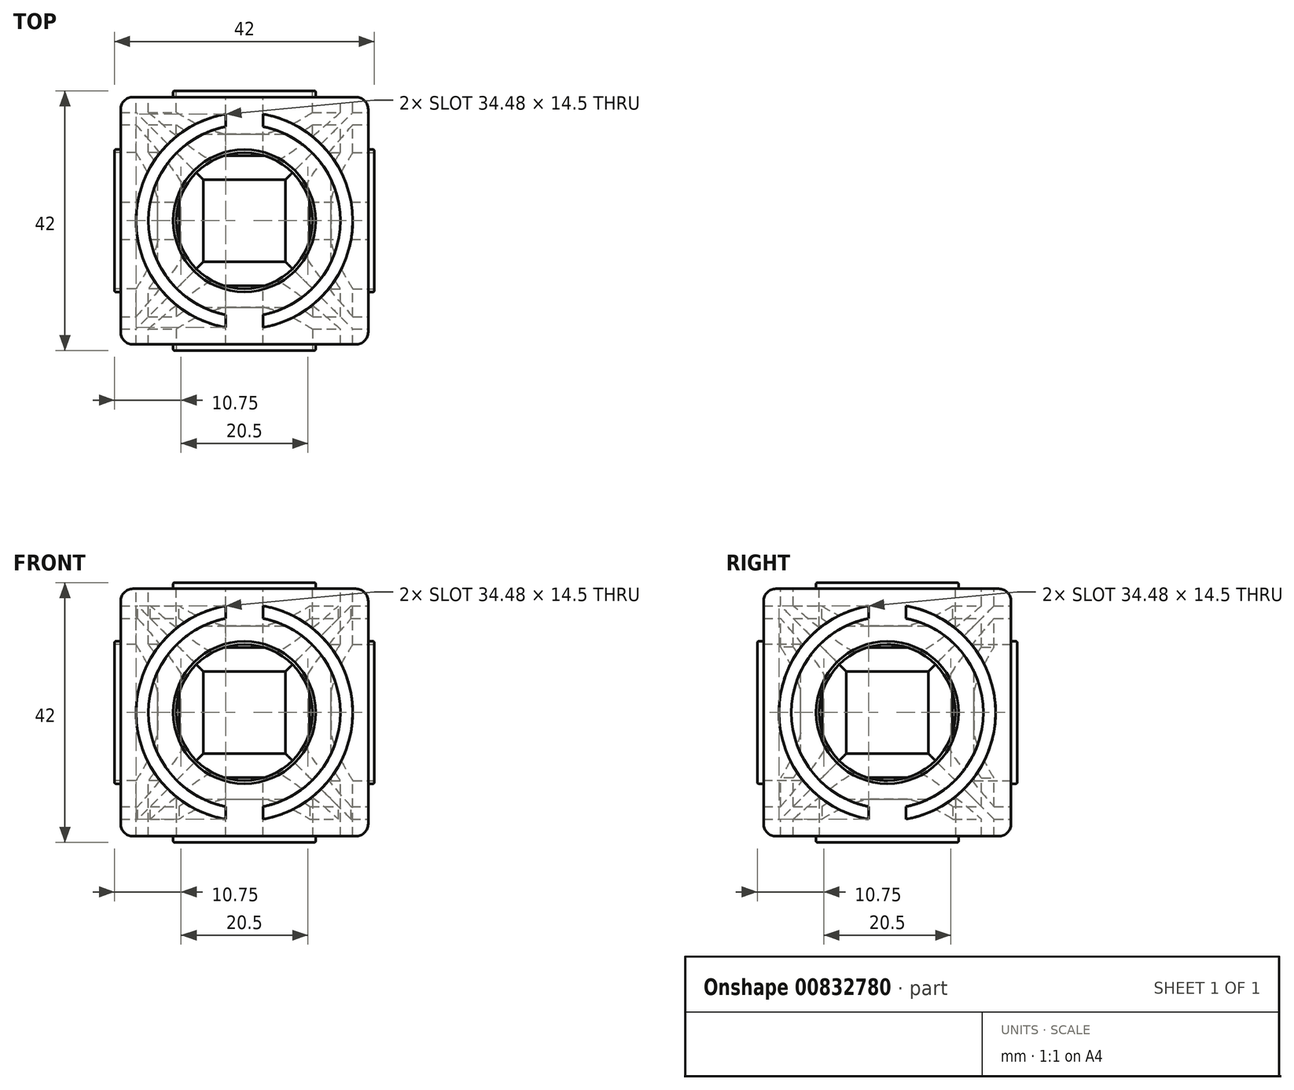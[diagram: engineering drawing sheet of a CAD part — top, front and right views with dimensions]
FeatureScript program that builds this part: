
annotation { "Feature Type Name" : "Feature", "Feature Type Description" : "" }
export const myFeature = defineFeature(function(context is Context, id is Id, definition is map)
    precondition{}
    {
        {
            var Q0;
            Q0=qCreatedBy(makeId("Top.planeOp"),FACE);
            var sketch = newSketch(context, id + "F0", { "sketchPlane" : qUnion([Q0])});
            skLineSegment(sketch, "E0", {"start": v(0, 20) * mm, "end": v(20, 20) * mm});
            skLineSegment(sketch, "E1", {"start": v(20, 20) * mm, "end": v(20, 0) * mm});
            skLineSegment(sketch, "E2", {"start": v(20, 0) * mm, "end": v(20, -20) * mm});
            skLineSegment(sketch, "E3.MirrorCS", {"start": v(-20, 0) * mm, "end": v(-20, -20) * mm});
            skLineSegment(sketch, "E4.MirrorCS", {"start": v(0, 20) * mm, "end": v(-20, 20) * mm});
            skLineSegment(sketch, "E5.MirrorCS", {"start": v(-20, -20) * mm, "end": v(0, -20) * mm});
            skLineSegment(sketch, "E6.MirrorCS", {"start": v(-20, 20) * mm, "end": v(-20, 0) * mm});
            skPoint(sketch, "E7.end.orphan", {"position": v(0, -20) * mm});
            skLineSegment(sketch, "E8.MirrorCS", {"start": v(20, -20) * mm, "end": v(0, -20) * mm});
            skSolve(sketch);
        }
        {
            var Q0;
            Q0 = qSketchRegion(id + "F0", true);
            extrude(context, id + "F1", {"entities" : qUnion([Q0]), "depth" : 40 * mm, "offsetDistance" : 25 * mm});
        }
        {
            var Q0;
            Q0=makeQuery(id+"F1.opExtrude","CAP_FACE",FACE,{"disambiguationData":[OSD([sQuery(id+"F0.wireOp",EDGE,"E0"),sQuery(id+"F0.wireOp",EDGE,"E1"),sQuery(id+"F0.wireOp",EDGE,"E2"),sQuery(id+"F0.wireOp",EDGE,"E3.MirrorCS"),sQuery(id+"F0.wireOp",EDGE,"E4.MirrorCS"),sQuery(id+"F0.wireOp",EDGE,"E5.MirrorCS"),sQuery(id+"F0.wireOp",EDGE,"E6.MirrorCS"),sQuery(id+"F0.wireOp",EDGE,"E8.MirrorCS")])],"isStart":true});
            var sketch = newSketch(context, id + "F2", { "sketchPlane" : qUnion([Q0])});
            skCircle(sketch, "E9", {"center": v(0, 0) * mm, "radius": 11 * mm});
            skSolve(sketch);
        }
        {
            var Q0;
            Q0 = qSketchRegion(id + "F2", true);
            extrude(context, id + "F3", {"entities" : qUnion([Q0]), "operationType" : NewBodyOperationType.REMOVE, "oppositeDirection" : true, "depth" : 6 * mm, "offsetDistance" : 25 * mm});
        }
        {
            var Q0;
            Q0=makeQuery(id+"F1.opExtrude","CAP_FACE",FACE,{"disambiguationData":[OSD([sQuery(id+"F0.wireOp",EDGE,"E0"),sQuery(id+"F0.wireOp",EDGE,"E1"),sQuery(id+"F0.wireOp",EDGE,"E2"),sQuery(id+"F0.wireOp",EDGE,"E3.MirrorCS"),sQuery(id+"F0.wireOp",EDGE,"E4.MirrorCS"),sQuery(id+"F0.wireOp",EDGE,"E5.MirrorCS"),sQuery(id+"F0.wireOp",EDGE,"E6.MirrorCS"),sQuery(id+"F0.wireOp",EDGE,"E8.MirrorCS")])],"isStart":false});
            var sketch = newSketch(context, id + "F4", { "sketchPlane" : qUnion([Q0])});
            skCircle(sketch, "E10", {"center": v(0, 0) * mm, "radius": 11 * mm});
            skSolve(sketch);
        }
        {
            var Q0;
            Q0 = qSketchRegion(id + "F4", true);
            extrude(context, id + "F5", {"entities" : qUnion([Q0]), "operationType" : NewBodyOperationType.REMOVE, "oppositeDirection" : true, "depth" : 6 * mm, "offsetDistance" : 25 * mm});
        }
        {
            var Q0;
            Q0=makeQuery(id+"F1.opExtrude","SWEPT_FACE",FACE,{"disambiguationData":[OSD([sQuery(id+"F0.wireOp",EDGE,"E5.MirrorCS"),sQuery(id+"F0.wireOp",EDGE,"E8.MirrorCS")])]});
            var sketch = newSketch(context, id + "F6", { "sketchPlane" : qUnion([Q0])});
            skCircle(sketch, "E11", {"center": v(0, 20) * mm, "radius": 11 * mm});
            skPoint(sketch, "E12.orphan", {"position": v(-20, 20) * mm});
            skPoint(sketch, "E13.end.orphan", {"position": v(20, 20) * mm});
            skPoint(sketch, "E14.start.orphan", {"position": v(0, 40) * mm});
            skSolve(sketch);
        }
        {
            var Q0;
            Q0 = qSketchRegion(id + "F6", true);
            extrude(context, id + "F7", {"entities" : qUnion([Q0]), "operationType" : NewBodyOperationType.REMOVE, "oppositeDirection" : true, "depth" : 6 * mm, "offsetDistance" : 25 * mm});
        }
        {
            var Q0;
            Q0=makeQuery(id+"F1.opExtrude","SWEPT_FACE",FACE,{"disambiguationData":[OSD([sQuery(id+"F0.wireOp",EDGE,"E1"),sQuery(id+"F0.wireOp",EDGE,"E2")])]});
            var sketch = newSketch(context, id + "F8", { "sketchPlane" : qUnion([Q0])});
            skCircle(sketch, "E15", {"center": v(0, 20) * mm, "radius": 11 * mm});
            skPoint(sketch, "E16.orphan", {"position": v(-20, 20) * mm});
            skPoint(sketch, "E17.start.orphan", {"position": v(0, 40) * mm});
            skPoint(sketch, "E18.end.orphan", {"position": v(20, 20) * mm});
            skSolve(sketch);
        }
        {
            var Q0;
            Q0 = qSketchRegion(id + "F8", true);
            extrude(context, id + "F9", {"entities" : qUnion([Q0]), "operationType" : NewBodyOperationType.REMOVE, "oppositeDirection" : true, "depth" : 6 * mm, "offsetDistance" : 25 * mm});
        }
        {
            var Q0;
            Q0=makeQuery(id+"F1.opExtrude","SWEPT_FACE",FACE,{"disambiguationData":[OSD([sQuery(id+"F0.wireOp",EDGE,"E0"),sQuery(id+"F0.wireOp",EDGE,"E4.MirrorCS")])]});
            var sketch = newSketch(context, id + "F10", { "sketchPlane" : qUnion([Q0])});
            skCircle(sketch, "E19", {"center": v(0, 20) * mm, "radius": 11 * mm});
            skPoint(sketch, "E20.orphan", {"position": v(-20, 20) * mm});
            skPoint(sketch, "E21.start.orphan", {"position": v(0, 40) * mm});
            skPoint(sketch, "E22.end.orphan", {"position": v(20, 20) * mm});
            skSolve(sketch);
        }
        {
            var Q0;
            Q0 = qSketchRegion(id + "F10", true);
            extrude(context, id + "F11", {"entities" : qUnion([Q0]), "operationType" : NewBodyOperationType.REMOVE, "oppositeDirection" : true, "depth" : 6 * mm, "offsetDistance" : 25 * mm});
        }
        {
            var Q0;
            Q0=makeQuery(id+"F1.opExtrude","SWEPT_FACE",FACE,{"disambiguationData":[OSD([sQuery(id+"F0.wireOp",EDGE,"E3.MirrorCS"),sQuery(id+"F0.wireOp",EDGE,"E6.MirrorCS")])]});
            var sketch = newSketch(context, id + "F12", { "sketchPlane" : qUnion([Q0])});
            skCircle(sketch, "E23", {"center": v(0, 20) * mm, "radius": 11 * mm});
            skPoint(sketch, "E24.orphan", {"position": v(-20, 20) * mm});
            skPoint(sketch, "E25.start.orphan", {"position": v(0, 40) * mm});
            skPoint(sketch, "E26.end.orphan", {"position": v(20, 20) * mm});
            skSolve(sketch);
        }
        {
            var Q0;
            Q0 = qSketchRegion(id + "F12", true);
            extrude(context, id + "F13", {"entities" : qUnion([Q0]), "operationType" : NewBodyOperationType.REMOVE, "oppositeDirection" : true, "depth" : 6 * mm, "offsetDistance" : 25 * mm});
        }
        {
            var Q0;
            Q0=makeQuery(id+"F4.imprint","IMPRINT",FACE,{"disambiguationData":[TD([[makeQuery(id+"F4.imprint","IMPRINT",EDGE,{"derivedFrom":sQuery(id+"F4.wireOp",EDGE,"E10")}),-1.0]])]});
            var sketch = newSketch(context, id + "F14", { "sketchPlane" : qUnion([Q0])});
            skArc(sketch, "E27", {"start": v(-3, 15.2) * mm, "mid": v(-15.5, 0) * mm, "end": v(-3, -15.2) * mm});
            skArc(sketch, "E28", {"start": v(-3, 17.24) * mm, "mid": v(-17.5, 0) * mm, "end": v(-3, -17.24) * mm});
            skLineSegment(sketch, "E29", {"start": v(3, 17.24) * mm, "end": v(3, 15.2) * mm});
            skLineSegment(sketch, "E30.MirrorCS", {"start": v(-3, 17.24) * mm, "end": v(-3, 15.2) * mm});
            skLineSegment(sketch, "E31.trimOffspring", {"start": v(-3, -15.2) * mm, "end": v(-3, -17.24) * mm});
            skLineSegment(sketch, "E32.trimOffspring", {"start": v(3, -15.2) * mm, "end": v(3, -17.24) * mm});
            skArc(sketch, "E33.trimOffspring", {"start": v(3, -15.2) * mm, "mid": v(15.5, 0) * mm, "end": v(3, 15.2) * mm});
            skArc(sketch, "E34.trimOffspring", {"start": v(3, -17.24) * mm, "mid": v(17.5, 0) * mm, "end": v(3, 17.24) * mm});
            skSolve(sketch);
        }
        {
            var Q0;
            Q0 = qSketchRegion(id + "F14", true);
            extrude(context, id + "F15", {"entities" : qUnion([Q0]), "operationType" : NewBodyOperationType.REMOVE, "oppositeDirection" : true, "depth" : 40 * mm, "offsetDistance" : 25 * mm});
        }
        {
            var Q0;
            Q0=makeQuery(id+"F1.opExtrude","SWEPT_FACE",FACE,{"disambiguationData":[OSD([sQuery(id+"F0.wireOp",EDGE,"E1"),sQuery(id+"F0.wireOp",EDGE,"E2")])]});
            var sketch = newSketch(context, id + "F16", { "sketchPlane" : qUnion([Q0])});
            skArc(sketch, "E35", {"start": v(-3, 35.2) * mm, "mid": v(-15.5, 20) * mm, "end": v(-3, 4.8) * mm});
            skArc(sketch, "E36", {"start": v(-3, 37.24) * mm, "mid": v(-17.5, 20) * mm, "end": v(-3, 2.76) * mm});
            skPoint(sketch, "E37.orphan", {"position": v(-20, 20) * mm});
            skPoint(sketch, "E38.trimOffspring.end.orphan", {"position": v(20, 20) * mm});
            skPoint(sketch, "E39.orphan", {"position": v(0, 40) * mm});
            skPoint(sketch, "E40.start.orphan", {"position": v(0, 0) * mm});
            skLineSegment(sketch, "E41", {"start": v(3, 37.24) * mm, "end": v(3, 35.2) * mm});
            skLineSegment(sketch, "E42.MirrorCS", {"start": v(-3, 37.24) * mm, "end": v(-3, 35.2) * mm});
            skLineSegment(sketch, "E43.trimOffspring", {"start": v(-3, 4.8) * mm, "end": v(-3, 2.76) * mm});
            skLineSegment(sketch, "E44.trimOffspring", {"start": v(3, 4.8) * mm, "end": v(3, 2.76) * mm});
            skArc(sketch, "E45.trimOffspring", {"start": v(3, 4.8) * mm, "mid": v(15.5, 20) * mm, "end": v(3, 35.2) * mm});
            skArc(sketch, "E46.trimOffspring", {"start": v(3, 2.76) * mm, "mid": v(17.5, 20) * mm, "end": v(3, 37.24) * mm});
            skSolve(sketch);
        }
        {
            var Q0;
            Q0 = qSketchRegion(id + "F16", true);
            extrude(context, id + "F17", {"entities" : qUnion([Q0]), "operationType" : NewBodyOperationType.REMOVE, "oppositeDirection" : true, "depth" : 40 * mm, "offsetDistance" : 25 * mm});
        }
        {
            var Q0;
            Q0=makeQuery(id+"F1.opExtrude","SWEPT_FACE",FACE,{"disambiguationData":[OSD([sQuery(id+"F0.wireOp",EDGE,"E0"),sQuery(id+"F0.wireOp",EDGE,"E4.MirrorCS")])]});
            var sketch = newSketch(context, id + "F18", { "sketchPlane" : qUnion([Q0])});
            skArc(sketch, "E47", {"start": v(3, 4.8) * mm, "mid": v(15.5, 20) * mm, "end": v(3, 35.2) * mm});
            skArc(sketch, "E48", {"start": v(3, 2.76) * mm, "mid": v(17.5, 20) * mm, "end": v(3, 37.24) * mm});
            skPoint(sketch, "E49.orphan", {"position": v(-20, 20) * mm});
            skPoint(sketch, "E50.end.orphan", {"position": v(20, 20) * mm});
            skPoint(sketch, "E51.orphan", {"position": v(0, 40) * mm});
            skPoint(sketch, "E52.end.orphan", {"position": v(0, 0) * mm});
            skLineSegment(sketch, "E53", {"start": v(3, 37.24) * mm, "end": v(3, 35.2) * mm});
            skLineSegment(sketch, "E54.MirrorCS", {"start": v(-3, 37.24) * mm, "end": v(-3, 35.2) * mm});
            skLineSegment(sketch, "E55.trimOffspring", {"start": v(3, 4.8) * mm, "end": v(3, 2.76) * mm});
            skLineSegment(sketch, "E56.trimOffspring", {"start": v(-3, 4.8) * mm, "end": v(-3, 2.76) * mm});
            skArc(sketch, "E57.trimOffspring", {"start": v(-3, 35.2) * mm, "mid": v(-15.5, 20) * mm, "end": v(-3, 4.8) * mm});
            skArc(sketch, "E58.trimOffspring", {"start": v(-3, 37.24) * mm, "mid": v(-17.5, 20) * mm, "end": v(-3, 2.76) * mm});
            skSolve(sketch);
        }
        {
            var Q0;
            Q0 = qSketchRegion(id + "F18", true);
            extrude(context, id + "F19", {"entities" : qUnion([Q0]), "operationType" : NewBodyOperationType.REMOVE, "oppositeDirection" : true, "depth" : 40 * mm, "offsetDistance" : 25 * mm});
        }
        {
            var Q0;
            Q0=makeQuery(id+"F4.imprint","IMPRINT",FACE,{"disambiguationData":[TD([[makeQuery(id+"F4.imprint","IMPRINT",EDGE,{"derivedFrom":sQuery(id+"F4.wireOp",EDGE,"E10")}),-1.0]])]});
            var sketch = newSketch(context, id + "F20", { "sketchPlane" : qUnion([Q0])});
            skCircle(sketch, "E59", {"center": v(0, 0) * mm, "radius": 11 * mm});
            skCircle(sketch, "E60", {"center": v(0, 0) * mm, "radius": 11.5 * mm});
            skSolve(sketch);
        }
        {
            var Q0;
            Q0 = qSketchRegion(id + "F20", true);
            extrude(context, id + "F21", {"entities" : qUnion([Q0]), "operationType" : NewBodyOperationType.ADD, "depth" : 1 * mm, "offsetDistance" : 25 * mm});
        }
        {
            var Q0;
            Q0=makeQuery(id+"F1.opExtrude","CAP_FACE",FACE,{"disambiguationData":[OSD([sQuery(id+"F0.wireOp",EDGE,"E0"),sQuery(id+"F0.wireOp",EDGE,"E1"),sQuery(id+"F0.wireOp",EDGE,"E2"),sQuery(id+"F0.wireOp",EDGE,"E3.MirrorCS"),sQuery(id+"F0.wireOp",EDGE,"E4.MirrorCS"),sQuery(id+"F0.wireOp",EDGE,"E5.MirrorCS"),sQuery(id+"F0.wireOp",EDGE,"E6.MirrorCS"),sQuery(id+"F0.wireOp",EDGE,"E8.MirrorCS")])],"isStart":true});
            var sketch = newSketch(context, id + "F22", { "sketchPlane" : qUnion([Q0])});
            skCircle(sketch, "E61", {"center": v(0, 0) * mm, "radius": 11 * mm});
            skCircle(sketch, "E62", {"center": v(0, 0) * mm, "radius": 11.5 * mm});
            skSolve(sketch);
        }
        {
            var Q0;
            Q0 = qSketchRegion(id + "F22", true);
            extrude(context, id + "F23", {"entities" : qUnion([Q0]), "operationType" : NewBodyOperationType.ADD, "depth" : 1 * mm, "offsetDistance" : 25 * mm});
        }
        {
            var Q0;
            Q0=makeQuery(id+"F1.opExtrude","SWEPT_FACE",FACE,{"disambiguationData":[OSD([sQuery(id+"F0.wireOp",EDGE,"E1"),sQuery(id+"F0.wireOp",EDGE,"E2")])]});
            var sketch = newSketch(context, id + "F24", { "sketchPlane" : qUnion([Q0])});
            skLineSegment(sketch, "E63", {"start": v(0, 40) * mm, "end": v(0, 0) * mm});
            skCircle(sketch, "E64", {"center": v(0, 20) * mm, "radius": 11 * mm});
            skCircle(sketch, "E65", {"center": v(0, 20) * mm, "radius": 11.5 * mm});
            skPoint(sketch, "E66.orphan", {"position": v(-20, 20) * mm});
            skPoint(sketch, "E67.end.orphan", {"position": v(20, 20) * mm});
            skSolve(sketch);
        }
        {
            var Q0;
            Q0 = qSketchRegion(id + "F24", true);
            extrude(context, id + "F25", {"entities" : qUnion([Q0]), "operationType" : NewBodyOperationType.ADD, "depth" : 1 * mm, "offsetDistance" : 25 * mm});
        }
        {
            var Q0;
            Q0=makeQuery(id+"F1.opExtrude","SWEPT_FACE",FACE,{"disambiguationData":[OSD([sQuery(id+"F0.wireOp",EDGE,"E5.MirrorCS"),sQuery(id+"F0.wireOp",EDGE,"E8.MirrorCS")])]});
            var sketch = newSketch(context, id + "F26", { "sketchPlane" : qUnion([Q0])});
            skCircle(sketch, "E68", {"center": v(0, 20) * mm, "radius": 11 * mm});
            skCircle(sketch, "E69", {"center": v(0, 20) * mm, "radius": 11.5 * mm});
            skPoint(sketch, "E70.orphan", {"position": v(-20, 20) * mm});
            skPoint(sketch, "E71.end.orphan", {"position": v(20, 20) * mm});
            skPoint(sketch, "E72.start.orphan", {"position": v(0, 40) * mm});
            skSolve(sketch);
        }
        {
            var Q0;
            Q0 = qSketchRegion(id + "F26", true);
            extrude(context, id + "F27", {"entities" : qUnion([Q0]), "operationType" : NewBodyOperationType.ADD, "depth" : 1 * mm, "offsetDistance" : 25 * mm});
        }
        {
            var Q0;
            Q0=makeQuery(id+"F1.opExtrude","SWEPT_FACE",FACE,{"disambiguationData":[OSD([sQuery(id+"F0.wireOp",EDGE,"E0"),sQuery(id+"F0.wireOp",EDGE,"E4.MirrorCS")])]});
            var sketch = newSketch(context, id + "F28", { "sketchPlane" : qUnion([Q0])});
            skCircle(sketch, "E73", {"center": v(0, 20) * mm, "radius": 11 * mm});
            skCircle(sketch, "E74", {"center": v(0, 20) * mm, "radius": 11.5 * mm});
            skPoint(sketch, "E75.end.orphan", {"position": v(20, 20) * mm});
            skPoint(sketch, "E76.trimOffspring.end.orphan", {"position": v(0, 0) * mm});
            skPoint(sketch, "E77.orphan", {"position": v(0, 40) * mm});
            skSolve(sketch);
        }
        {
            var Q0;
            Q0 = qSketchRegion(id + "F28", true);
            extrude(context, id + "F29", {"entities" : qUnion([Q0]), "operationType" : NewBodyOperationType.ADD, "depth" : 1 * mm, "offsetDistance" : 25 * mm});
        }
        {
            var Q0;
            Q0=makeQuery(id+"F1.opExtrude","SWEPT_FACE",FACE,{"disambiguationData":[OSD([sQuery(id+"F0.wireOp",EDGE,"E3.MirrorCS"),sQuery(id+"F0.wireOp",EDGE,"E6.MirrorCS")])]});
            var sketch = newSketch(context, id + "F30", { "sketchPlane" : qUnion([Q0])});
            skCircle(sketch, "E78", {"center": v(0, 20) * mm, "radius": 11 * mm});
            skCircle(sketch, "E79", {"center": v(0, 20) * mm, "radius": 11.5 * mm});
            skPoint(sketch, "E80.orphan", {"position": v(-20, 20) * mm});
            skPoint(sketch, "E81.end.orphan", {"position": v(20, 20) * mm});
            skPoint(sketch, "E82.trimOffspring.end.orphan", {"position": v(0, 0) * mm});
            skPoint(sketch, "E83.start.orphan", {"position": v(0, 40) * mm});
            skSolve(sketch);
        }
        {
            var Q0;
            Q0 = qSketchRegion(id + "F30", true);
            extrude(context, id + "F31", {"entities" : qUnion([Q0]), "operationType" : NewBodyOperationType.ADD, "depth" : 1 * mm, "offsetDistance" : 25 * mm});
        }
        {
            var Q0;
            Q0=makeQuery(id+"F1.opExtrude","CAP_EDGE",EDGE,{"disambiguationData":[OSD([sQuery(id+"F0.wireOp",EDGE,"E5.MirrorCS"),sQuery(id+"F0.wireOp",EDGE,"E8.MirrorCS")])],"isStart":false});
            var Q1;
            Q1=makeQuery(id+"F1.opExtrude","SWEPT_EDGE",EDGE,{"disambiguationData":[OSD([sQuery(id+"F0.wireOp",EDGE,"E3.MirrorCS"),sQuery(id+"F0.wireOp",EDGE,"E5.MirrorCS")])]});
            var Q2;
            Q2=makeQuery(id+"F1.opExtrude","SWEPT_EDGE",EDGE,{"disambiguationData":[OSD([sQuery(id+"F0.wireOp",EDGE,"E2"),sQuery(id+"F0.wireOp",EDGE,"E8.MirrorCS")])]});
            var Q3;
            Q3=makeQuery(id+"F1.opExtrude","CAP_EDGE",EDGE,{"disambiguationData":[OSD([sQuery(id+"F0.wireOp",EDGE,"E3.MirrorCS"),sQuery(id+"F0.wireOp",EDGE,"E6.MirrorCS")])],"isStart":true});
            var Q4;
            Q4=makeQuery(id+"F1.opExtrude","CAP_EDGE",EDGE,{"disambiguationData":[OSD([sQuery(id+"F0.wireOp",EDGE,"E1"),sQuery(id+"F0.wireOp",EDGE,"E2")])],"isStart":true});
            var Q5;
            Q5=makeQuery(id+"F1.opExtrude","CAP_EDGE",EDGE,{"disambiguationData":[OSD([sQuery(id+"F0.wireOp",EDGE,"E0"),sQuery(id+"F0.wireOp",EDGE,"E4.MirrorCS")])],"isStart":true});
            var Q6;
            Q6=makeQuery(id+"F1.opExtrude","SWEPT_EDGE",EDGE,{"disambiguationData":[OSD([sQuery(id+"F0.wireOp",EDGE,"E0"),sQuery(id+"F0.wireOp",EDGE,"E1")])]});
            var Q7;
            Q7=makeQuery(id+"F1.opExtrude","SWEPT_EDGE",EDGE,{"disambiguationData":[OSD([sQuery(id+"F0.wireOp",EDGE,"E4.MirrorCS"),sQuery(id+"F0.wireOp",EDGE,"E6.MirrorCS")])]});
            var Q8;
            Q8=makeQuery(id+"F1.opExtrude","CAP_EDGE",EDGE,{"disambiguationData":[OSD([sQuery(id+"F0.wireOp",EDGE,"E0"),sQuery(id+"F0.wireOp",EDGE,"E4.MirrorCS")])],"isStart":false});
            var Q9;
            Q9=makeQuery(id+"F1.opExtrude","CAP_EDGE",EDGE,{"disambiguationData":[OSD([sQuery(id+"F0.wireOp",EDGE,"E1"),sQuery(id+"F0.wireOp",EDGE,"E2")])],"isStart":false});
            var Q10;
            Q10=makeQuery(id+"F1.opExtrude","CAP_EDGE",EDGE,{"disambiguationData":[OSD([sQuery(id+"F0.wireOp",EDGE,"E3.MirrorCS"),sQuery(id+"F0.wireOp",EDGE,"E6.MirrorCS")])],"isStart":false});
            var Q11;
            Q11=makeQuery(id+"F1.opExtrude","CAP_EDGE",EDGE,{"disambiguationData":[OSD([sQuery(id+"F0.wireOp",EDGE,"E5.MirrorCS"),sQuery(id+"F0.wireOp",EDGE,"E8.MirrorCS")])],"isStart":true});
            fillet(context, id + "F32", {"entities" : qUnion([Q0, Q1, Q2, Q3, Q4, Q5, Q6, Q7, Q8, Q9, Q10, Q11]), "radius" : 2 * mm, "tangentPropagation" : true, "allowEdgeOverflow" : false});
        }
        {
            var Q0;
            Q0=makeQuery(id+"F31.opExtrude","CAP_EDGE",EDGE,{"disambiguationData":[OSD([sQuery(id+"F30.wireOp",EDGE,"E79")])],"isStart":false});
            var Q1;
            Q1=makeQuery(id+"F31.opExtrude","CAP_EDGE",EDGE,{"disambiguationData":[OSD([sQuery(id+"F30.wireOp",EDGE,"E78")])],"isStart":false});
            var Q2;
            Q2=makeQuery(id+"F27.opExtrude","CAP_EDGE",EDGE,{"disambiguationData":[OSD([sQuery(id+"F26.wireOp",EDGE,"E69")])],"isStart":false});
            var Q3;
            Q3=makeQuery(id+"F27.opExtrude","CAP_EDGE",EDGE,{"disambiguationData":[OSD([sQuery(id+"F26.wireOp",EDGE,"E68")])],"isStart":false});
            var Q4;
            Q4=makeQuery(id+"F25.opExtrude","CAP_EDGE",EDGE,{"disambiguationData":[OSD([sQuery(id+"F24.wireOp",EDGE,"E65")])],"isStart":false});
            var Q5;
            Q5=makeQuery(id+"F25.opExtrude","CAP_EDGE",EDGE,{"disambiguationData":[OSD([sQuery(id+"F24.wireOp",EDGE,"E64")])],"isStart":false});
            var Q6;
            Q6=makeQuery(id+"F29.opExtrude","CAP_EDGE",EDGE,{"disambiguationData":[OSD([sQuery(id+"F28.wireOp",EDGE,"E74")])],"isStart":false});
            var Q7;
            Q7=makeQuery(id+"F29.opExtrude","CAP_EDGE",EDGE,{"disambiguationData":[OSD([sQuery(id+"F28.wireOp",EDGE,"E73")])],"isStart":false});
            var Q8;
            Q8=makeQuery(id+"F21.opExtrude","CAP_EDGE",EDGE,{"disambiguationData":[OSD([sQuery(id+"F20.wireOp",EDGE,"E60")])],"isStart":false});
            var Q9;
            Q9=makeQuery(id+"F21.opExtrude","CAP_EDGE",EDGE,{"disambiguationData":[OSD([sQuery(id+"F20.wireOp",EDGE,"E59")])],"isStart":false});
            var Q10;
            Q10=makeQuery(id+"F23.opExtrude","CAP_EDGE",EDGE,{"disambiguationData":[OSD([sQuery(id+"F22.wireOp",EDGE,"E62")])],"isStart":false});
            var Q11;
            Q11=makeQuery(id+"F23.opExtrude","CAP_EDGE",EDGE,{"disambiguationData":[OSD([sQuery(id+"F22.wireOp",EDGE,"E61")])],"isStart":false});
            fillet(context, id + "F33", {"entities" : qUnion([Q0, Q1, Q2, Q3, Q4, Q5, Q6, Q7, Q8, Q9, Q10, Q11]), "radius" : 0.2 * mm, "tangentPropagation" : true, "allowEdgeOverflow" : false});
        }
    });
